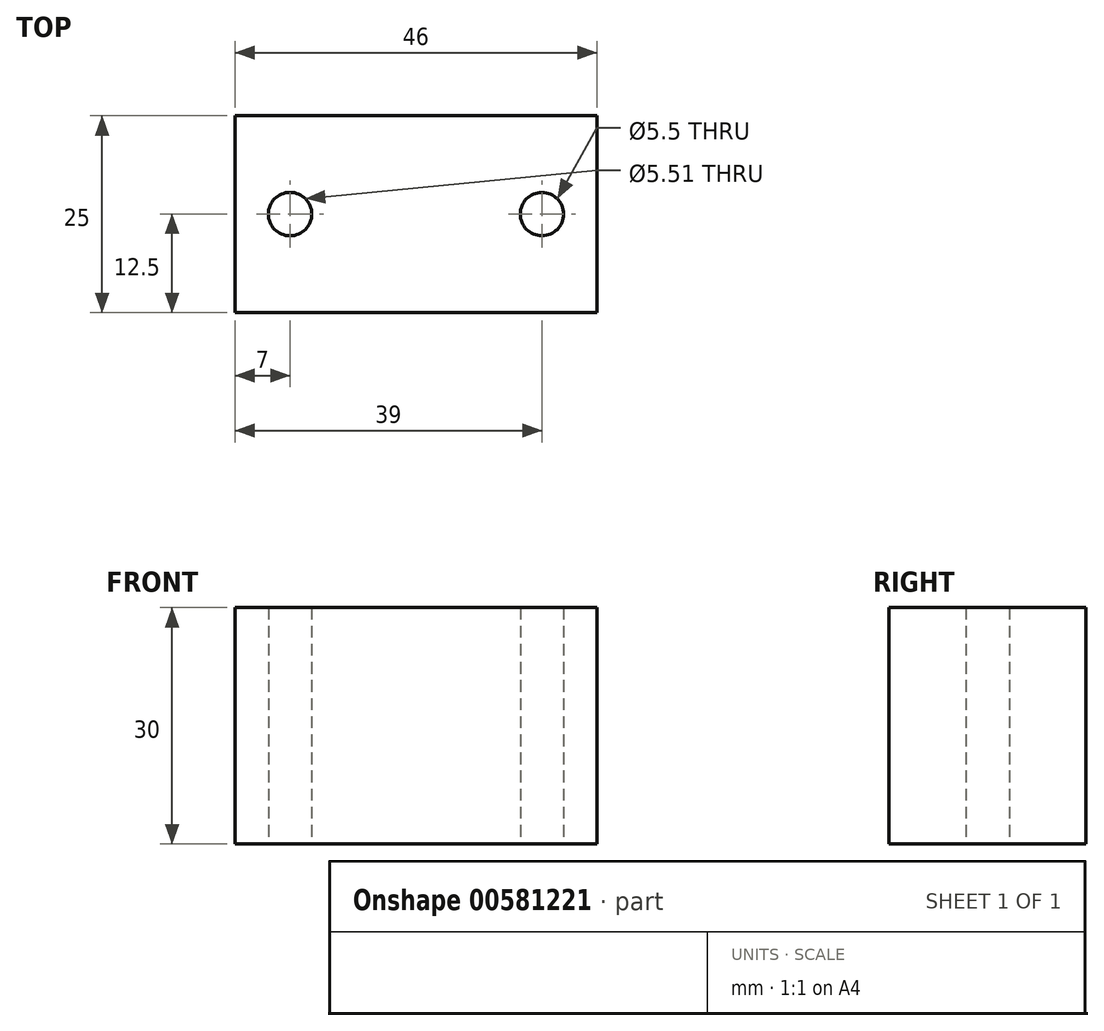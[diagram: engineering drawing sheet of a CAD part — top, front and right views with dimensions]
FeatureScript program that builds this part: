
annotation { "Feature Type Name" : "Feature", "Feature Type Description" : "" }
export const myFeature = defineFeature(function(context is Context, id is Id, definition is map)
    precondition{}
    {
        {
            var Q0;
            Q0=qCreatedBy(makeId("Top.planeOp"),FACE);
            var sketch = newSketch(context, id + "F0", { "sketchPlane" : qUnion([Q0])});
            skLineSegment(sketch, "E0.bottom", {"start": v(23, 12.5) * mm, "end": v(-23, 12.5) * mm});
            skLineSegment(sketch, "E0.top", {"start": v(23, -12.5) * mm, "end": v(-23, -12.5) * mm});
            skLineSegment(sketch, "E0.left", {"start": v(23, 12.5) * mm, "end": v(23, -12.5) * mm});
            skLineSegment(sketch, "E0.right", {"start": v(-23, 12.5) * mm, "end": v(-23, -12.5) * mm});
            skPoint(sketch, "E0.middle", {"position": v(0, 0) * mm});
            skCircle(sketch, "E1", {"center": v(16, 0) * mm, "radius": 2.75 * mm});
            skCircle(sketch, "E2.MirrorC", {"center": v(-16, 0) * mm, "radius": 2.76 * mm});
            skSolve(sketch);
        }
        {
            var Q0;
            Q0=qSketchRegion(id+"F0",true);
            extrude(context, id + "F1", {"entities" : qUnion([Q0]), "depth" : 30 * mm, "offsetDistance" : 25.4 * mm});
        }
    });
